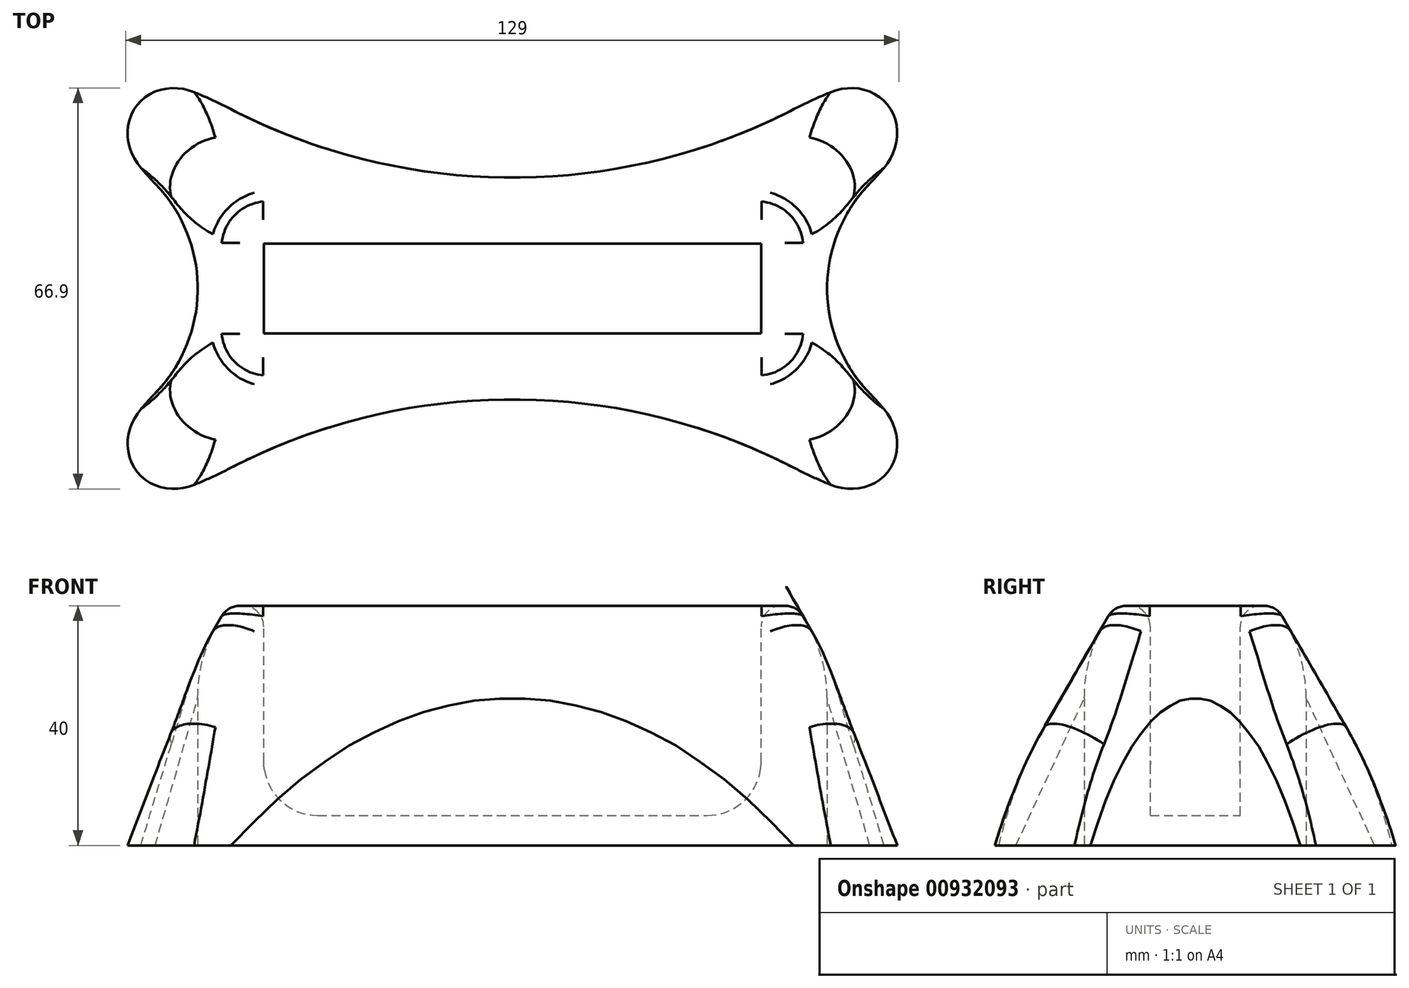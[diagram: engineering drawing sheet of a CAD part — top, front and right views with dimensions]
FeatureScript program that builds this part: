
annotation { "Feature Type Name" : "Feature", "Feature Type Description" : "" }
export const myFeature = defineFeature(function(context is Context, id is Id, definition is map)
    precondition{}
    {
        {
            var Q0;
            Q0=qCreatedBy(makeId("Right.planeOp"),FACE);
            var sketch = newSketch(context, id + "F0", { "sketchPlane" : qUnion([Q0])});
            skLineSegment(sketch, "E0", {"start": v(-36.6, 0) * mm, "end": v(36.6, 0) * mm});
            skLineSegment(sketch, "E1", {"start": v(36.6, 0) * mm, "end": v(13.5, 40) * mm});
            skLineSegment(sketch, "E2", {"start": v(13.5, 40) * mm, "end": v(-13.5, 40) * mm});
            skLineSegment(sketch, "E3", {"start": v(-13.5, 40) * mm, "end": v(-36.6, 0) * mm});
            skLineSegment(sketch, "E4", {"start": v(0, 0) * mm, "end": v(0, 40) * mm, "construction": true});
            skPoint(sketch, "E5.orphan", {"position": v(-36.6, 0) * mm});
            skPoint(sketch, "E6.visualSharp", {"position": v(-13.5, 40) * mm});
            skPoint(sketch, "E7.visualSharp", {"position": v(13.5, 40) * mm});
            skSolve(sketch);
        }
        {
            var Q0;
            Q0=makeQuery(id+"F0.imprint","IMPRINT",FACE,{"disambiguationData":[TD([[makeQuery(id+"F0.imprint","IMPRINT",EDGE,{"derivedFrom":sQuery(id+"F0.wireOp",EDGE,"E0")}),1.0]])]});
            extrude(context, id + "F1", {"entities" : qUnion([Q0]), "endBound" : BoundingType.SYMMETRIC, "depth" : 95 * mm, "offsetDistance" : 25.4 * mm});
        }
        {
            var Q0;
            Q0=makeQuery(id+"F1.opExtrude","SWEPT_FACE",FACE,{"disambiguationData":[OSD([sQuery(id+"F0.wireOp",EDGE,"E2")])]});
            var sketch = newSketch(context, id + "F2", { "sketchPlane" : qUnion([Q0])});
            skLineSegment(sketch, "E8.bottom", {"start": v(-41.4, -7.5) * mm, "end": v(41.4, -7.5) * mm});
            skLineSegment(sketch, "E8.top", {"start": v(-41.4, 7.5) * mm, "end": v(41.4, 7.5) * mm});
            skLineSegment(sketch, "E8.left", {"start": v(-41.5, -7.4) * mm, "end": v(-41.5, 7.4) * mm});
            skLineSegment(sketch, "E8.right", {"start": v(41.5, -7.4) * mm, "end": v(41.5, 7.4) * mm});
            skPoint(sketch, "E9.visualSharp", {"position": v(-41.5, 7.5) * mm});
            skArc(sketch, "E9.filletArc", {"start": v(-41.4, 7.5) * mm, "mid": v(-41.47, 7.47) * mm, "end": v(-41.5, 7.4) * mm});
            skPoint(sketch, "E10.visualSharp", {"position": v(41.5, 7.5) * mm});
            skArc(sketch, "E10.filletArc", {"start": v(41.5, 7.4) * mm, "mid": v(41.47, 7.47) * mm, "end": v(41.4, 7.5) * mm});
            skPoint(sketch, "E11.visualSharp", {"position": v(41.5, -7.5) * mm});
            skArc(sketch, "E11.filletArc", {"start": v(41.4, -7.5) * mm, "mid": v(41.47, -7.47) * mm, "end": v(41.5, -7.4) * mm});
            skPoint(sketch, "E12.visualSharp", {"position": v(-41.5, -7.5) * mm});
            skArc(sketch, "E12.filletArc", {"start": v(-41.5, -7.4) * mm, "mid": v(-41.47, -7.47) * mm, "end": v(-41.4, -7.5) * mm});
            skSolve(sketch);
        }
        {
            var Q0;
            Q0 = qSketchRegion(id + "F2", true);
            extrude(context, id + "F3", {"entities" : qUnion([Q0]), "operationType" : NewBodyOperationType.REMOVE, "oppositeDirection" : true, "depth" : 35 * mm, "offsetDistance" : 25.4 * mm});
        }
        {
            var Q0;
            Q0=qCreatedBy(makeId("Front.planeOp"),FACE);
            var sketch = newSketch(context, id + "F4", { "sketchPlane" : qUnion([Q0])});
            skLineSegment(sketch, "E13", {"start": v(-47.5, 40) * mm, "end": v(-70.6, 0) * mm});
            skLineSegment(sketch, "E14", {"start": v(-70.6, 0) * mm, "end": v(-47.5, 0) * mm});
            skLineSegment(sketch, "E15", {"start": v(-47.5, 0) * mm, "end": v(-47.5, 40) * mm});
            skLineSegment(sketch, "E16.MirrorCS", {"start": v(47.5, 0) * mm, "end": v(47.5, 40) * mm});
            skLineSegment(sketch, "E17.MirrorCS", {"start": v(47.5, 40) * mm, "end": v(70.6, 0) * mm});
            skLineSegment(sketch, "E18.MirrorCS", {"start": v(70.6, 0) * mm, "end": v(47.5, 0) * mm});
            skSolve(sketch);
        }
        {
            var Q0;
            Q0 = qSketchRegion(id + "F4", true);
            var Q1;
            Q1=makeQuery(id+"F1.opExtrude","SWEPT_FACE",FACE,{"disambiguationData":[OSD([sQuery(id+"F0.wireOp",EDGE,"E3")])]});
            extrude(context, id + "F5", {"entities" : qUnion([Q0]), "operationType" : NewBodyOperationType.ADD, "endBound" : BoundingType.UP_TO_SURFACE, "depth" : 25.4 * mm, "endBoundEntityFace" : qUnion([Q1]), "offsetDistance" : 25.4 * mm});
        }
        {
            var Q0;
            Q0 = qSketchRegion(id + "F4", true);
            var Q1;
            Q1=makeQuery(id+"F1.opExtrude","SWEPT_FACE",FACE,{"disambiguationData":[OSD([sQuery(id+"F0.wireOp",EDGE,"E1")])]});
            extrude(context, id + "F6", {"entities" : qUnion([Q0]), "operationType" : NewBodyOperationType.ADD, "endBound" : BoundingType.UP_TO_SURFACE, "oppositeDirection" : true, "depth" : 25.4 * mm, "endBoundEntityFace" : qUnion([Q1]), "offsetDistance" : 25.4 * mm});
        }
        {
            var Q0;
            Q0=makeQuery(id+"F1.opExtrude","SWEPT_FACE",FACE,{"disambiguationData":[OSD([sQuery(id+"F0.wireOp",EDGE,"E0")])]});
            var sketch = newSketch(context, id + "F7", { "sketchPlane" : qUnion([Q0])});
            skCircle(sketch, "E19", {"center": v(0, 120.8) * mm, "radius": 102.3 * mm});
            skCircle(sketch, "E20.MirrorC", {"center": v(0, -120.8) * mm, "radius": 102.3 * mm});
            skCircle(sketch, "E21", {"center": v(77.59, 0) * mm, "radius": 25.09 * mm});
            skCircle(sketch, "E22.MirrorC", {"center": v(-77.59, 0) * mm, "radius": 25.09 * mm});
            skPoint(sketch, "E23", {"position": v(-70.6, 24.1) * mm});
            skPoint(sketch, "E24", {"position": v(-58.1, 36.6) * mm});
            skSolve(sketch);
        }
        {
            var Q0;
            Q0 = qSketchRegion(id + "F7", true);
            extrude(context, id + "F8", {"entities" : qUnion([Q0]), "operationType" : NewBodyOperationType.REMOVE, "endBound" : BoundingType.THROUGH_ALL, "oppositeDirection" : true, "depth" : 25.4 * mm, "offsetDistance" : 25.4 * mm});
        }
        {
            var Q0;
            Q0=makeQuery(id+"F8.boolean.opBoolean","INTERSECT",EDGE,{"derivedFrom":[makeQuery(id+"F1.opExtrude","SWEPT_FACE",FACE,{"disambiguationData":[OSD([sQuery(id+"F0.wireOp",EDGE,"E1")])]}),makeQuery(id+"F8.opExtrude","SWEPT_FACE",FACE,{"disambiguationData":[OSD([sQuery(id+"F7.wireOp",EDGE,"E20.MirrorC")])]})]});
            var Q1;
            Q1=makeQuery(id+"F8.boolean.opBoolean","INTERSECT",EDGE,{"derivedFrom":[makeQuery(id+"F1.opExtrude","SWEPT_FACE",FACE,{"disambiguationData":[OSD([sQuery(id+"F0.wireOp",EDGE,"E3")])]}),makeQuery(id+"F8.opExtrude","SWEPT_FACE",FACE,{"disambiguationData":[OSD([sQuery(id+"F7.wireOp",EDGE,"E19")])]})]});
            var Q2;
            {var subQ0=sQuery(id+"F4.wireOp",EDGE,"E13");Q2=makeQuery(id+"F8.boolean.opBoolean","INTERSECT",EDGE,{"derivedFrom":[makeQuery(id+"F6.boolean.opBoolean","MERGE",FACE,{"derivedFrom":[makeQuery(id+"F5.opExtrude","SWEPT_FACE",FACE,{"disambiguationData":[OSD([subQ0])]}),makeQuery(id+"F6.opExtrude","SWEPT_FACE",FACE,{"disambiguationData":[OSD([subQ0])]})]}),makeQuery(id+"F8.opExtrude","SWEPT_FACE",FACE,{"disambiguationData":[OSD([sQuery(id+"F7.wireOp",EDGE,"E22.MirrorC")])]})]});}
            var Q3;
            {var subQ0=sQuery(id+"F4.wireOp",EDGE,"E17.MirrorCS");Q3=makeQuery(id+"F8.boolean.opBoolean","INTERSECT",EDGE,{"derivedFrom":[makeQuery(id+"F6.boolean.opBoolean","MERGE",FACE,{"derivedFrom":[makeQuery(id+"F5.opExtrude","SWEPT_FACE",FACE,{"disambiguationData":[OSD([subQ0])]}),makeQuery(id+"F6.opExtrude","SWEPT_FACE",FACE,{"disambiguationData":[OSD([subQ0])]})]}),makeQuery(id+"F8.opExtrude","SWEPT_FACE",FACE,{"disambiguationData":[OSD([sQuery(id+"F7.wireOp",EDGE,"E21")])]})]});}
            fillet(context, id + "F9", {"entities" : qUnion([Q0, Q1, Q2, Q3]), "radius" : 25 * mm, "tangentPropagation" : true, "allowEdgeOverflow" : false});
        }
        {
            var Q0;
            Q0=makeQuery(id+"F9.opFillet","BLEND_EDGE",EDGE,{"blendedFrom":[makeQuery(id+"F8.boolean.opBoolean","INTERSECT",EDGE,{"derivedFrom":[makeQuery(id+"F1.opExtrude","SWEPT_FACE",FACE,{"disambiguationData":[OSD([sQuery(id+"F0.wireOp",EDGE,"E3")])]}),makeQuery(id+"F8.opExtrude","SWEPT_FACE",FACE,{"disambiguationData":[OSD([sQuery(id+"F7.wireOp",EDGE,"E19")])]})]}),makeQuery(id+"FT0I9snNkOnfvNE_1.boolean.opBoolean","COPY",FACE,{"derivedFrom":makeQuery(id+"FT0I9snNkOnfvNE_1.opExtrude","SWEPT_FACE",FACE,{"disambiguationData":[OSD([sQuery(id+"FyN7Zmtp0H1jUXP_1.wireOp",EDGE,"ABEdghNr-eVXP-MfwK-tvM9-xuFfk5gp8r2I")])]})})],"blendedInto":[makeQuery(id+"FT0I9snNkOnfvNE_1.boolean.opBoolean","COPY",FACE,{"derivedFrom":makeQuery(id+"FT0I9snNkOnfvNE_1.opExtrude","SWEPT_FACE",FACE,{"disambiguationData":[OSD([sQuery(id+"FyN7Zmtp0H1jUXP_1.wireOp",EDGE,"ABEdghNr-eVXP-MfwK-tvM9-xuFfk5gp8r2I")])]})})]});
            var Q1;
            Q1=makeQuery(id+"F1.opExtrude","CAP_EDGE",EDGE,{"disambiguationData":[OSD([sQuery(id+"F0.wireOp",EDGE,"E1")])],"isStart":false});
            var Q2;
            Q2=makeQuery(id+"FT0I9snNkOnfvNE_1.boolean.opBoolean","INTERSECT",EDGE,{"derivedFrom":[makeQuery(id+"F1.opExtrude","SWEPT_FACE",FACE,{"disambiguationData":[OSD([sQuery(id+"F0.wireOp",EDGE,"E1")])]}),makeQuery(id+"FT0I9snNkOnfvNE_1.opExtrude","SWEPT_FACE",FACE,{"disambiguationData":[OSD([sQuery(id+"FyN7Zmtp0H1jUXP_1.wireOp",EDGE,"cfb1d19c-3061-4cc1-8817-f68da6fe64092.MirrorCS")])]})]});
            var Q3;
            Q3=makeQuery(id+"FT0I9snNkOnfvNE_1.boolean.opBoolean","INTERSECT",EDGE,{"derivedFrom":[makeQuery(id+"F1.opExtrude","SWEPT_FACE",FACE,{"disambiguationData":[OSD([sQuery(id+"F0.wireOp",EDGE,"E3")])]}),makeQuery(id+"FT0I9snNkOnfvNE_1.opExtrude","SWEPT_FACE",FACE,{"disambiguationData":[OSD([sQuery(id+"FyN7Zmtp0H1jUXP_1.wireOp",EDGE,"cfb1d19c-3061-4cc1-8817-f68da6fe64093.MirrorCS")])]})]});
            var Q4;
            Q4=makeQuery(id+"F6.opExtrude","CAP_EDGE",EDGE,{"disambiguationData":[OSD([sQuery(id+"F4.wireOp",EDGE,"E13")])],"isStart":false});
            var Q5;
            Q5=makeQuery(id+"F5.opExtrude","CAP_EDGE",EDGE,{"disambiguationData":[OSD([sQuery(id+"F4.wireOp",EDGE,"E13")])],"isStart":false});
            var Q6;
            Q6=makeQuery(id+"F5.opExtrude","CAP_EDGE",EDGE,{"disambiguationData":[OSD([sQuery(id+"F4.wireOp",EDGE,"E17.MirrorCS")])],"isStart":false});
            var Q7;
            Q7=makeQuery(id+"F6.opExtrude","CAP_EDGE",EDGE,{"disambiguationData":[OSD([sQuery(id+"F4.wireOp",EDGE,"E17.MirrorCS")])],"isStart":false});
            fillet(context, id + "F10", {"entities" : qUnion([Q0, Q1, Q2, Q3, Q4, Q5, Q6, Q7]), "radius" : 8 * mm, "tangentPropagation" : true, "allowEdgeOverflow" : false});
        }
        {
            var Q0;
            Q0=makeQuery(id+"F1.opExtrude","SWEPT_FACE",FACE,{"disambiguationData":[OSD([sQuery(id+"F0.wireOp",EDGE,"E2")])]});
            fillet(context, id + "F11", {"entities" : qUnion([Q0]), "radius" : 3.5 * mm, "allowEdgeOverflow" : false});
        }
        {
            var Q0;
            Q0=makeQuery(id+"F3.boolean.opBoolean","COPY",EDGE,{"derivedFrom":makeQuery(id+"F3.opExtrude","CAP_EDGE",EDGE,{"disambiguationData":[OSD([sQuery(id+"F2.wireOp",EDGE,"E8.left")])],"isStart":false})});
            var Q1;
            Q1=makeQuery(id+"F3.boolean.opBoolean","COPY",EDGE,{"derivedFrom":makeQuery(id+"F3.opExtrude","CAP_EDGE",EDGE,{"disambiguationData":[OSD([sQuery(id+"F2.wireOp",EDGE,"E8.right")])],"isStart":false})});
            fillet(context, id + "F12", {"entities" : qUnion([Q0, Q1]), "radius" : 9 * mm, "allowEdgeOverflow" : false});
        }
    });
